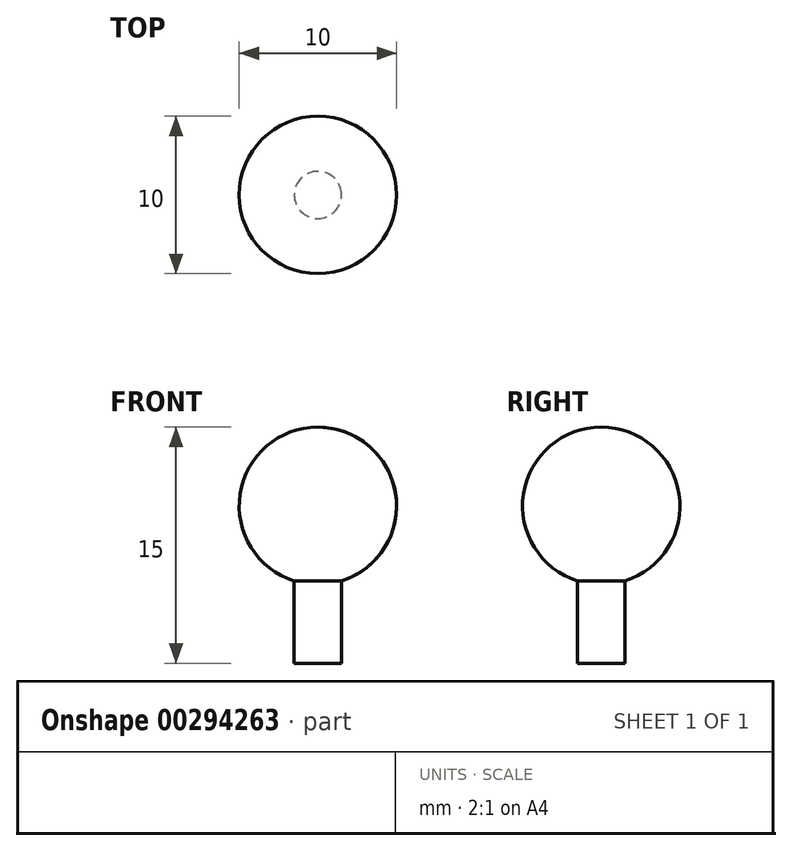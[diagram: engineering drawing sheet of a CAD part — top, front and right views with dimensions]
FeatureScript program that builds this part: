
annotation { "Feature Type Name" : "Feature", "Feature Type Description" : "" }
export const myFeature = defineFeature(function(context is Context, id is Id, definition is map)
    precondition{}
    {
        {
            var Q0;
            Q0=qCreatedBy(makeId("Front.planeOp"),FACE);
            var sketch = newSketch(context, id + "F0", { "sketchPlane" : qUnion([Q0])});
            skArc(sketch, "E0", {"start": v(1.5, -4.77) * mm, "mid": v(4.94, 0.76) * mm, "end": v(0, 5) * mm});
            skLineSegment(sketch, "E1.bottom", {"start": v(0, -10) * mm, "end": v(1.5, -10) * mm});
            skLineSegment(sketch, "E1.right", {"start": v(1.5, -10) * mm, "end": v(1.5, -4.77) * mm});
            skPoint(sketch, "E1.top.start.orphan", {"position": v(-1.5, 10) * mm});
            skPoint(sketch, "E2.trimOffspring.end.orphan", {"position": v(1.5, 15.24) * mm});
            skLineSegment(sketch, "E3", {"start": v(0, 5) * mm, "end": v(0, -10) * mm});
            skSolve(sketch);
        }
        {
            var Q0;
            Q0 = qSketchRegion(id + "F0", true);
            var Q1;
            Q1=sQuery(id+"F0.wireOp",EDGE,"E3");
            revolve(context, id + "F1", {"entities" : qUnion([Q0]), "axis" : qUnion([Q1]), "revolveType" : RevolveType.FULL});
        }
    });
